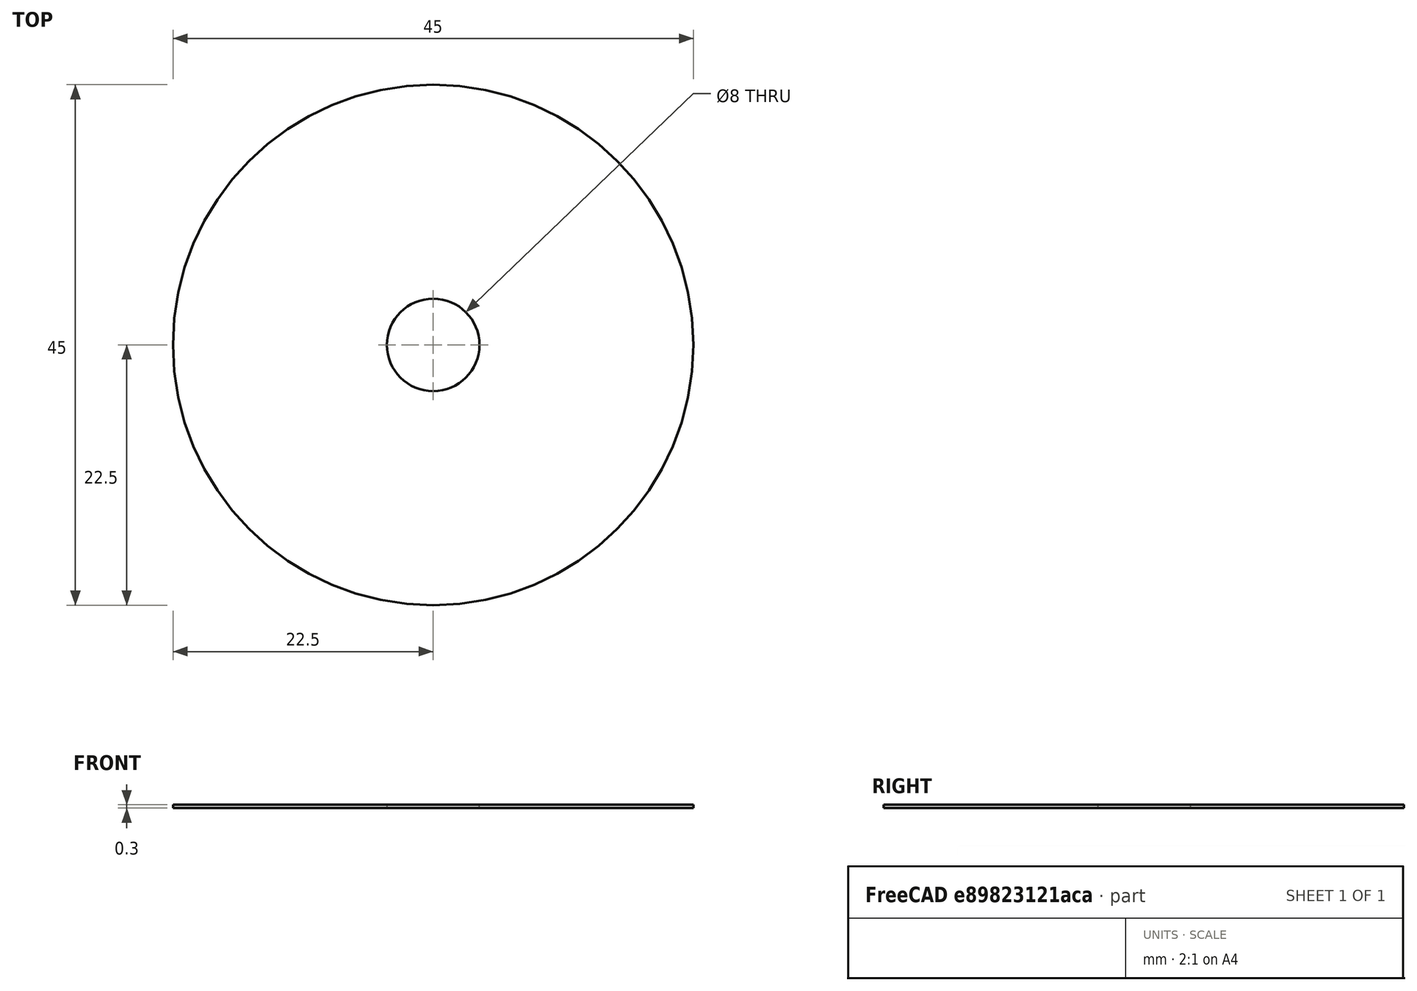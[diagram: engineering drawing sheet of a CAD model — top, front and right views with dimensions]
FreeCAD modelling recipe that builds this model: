
FCSTD DOCUMENT  (FreeCAD 1.0R39109 (Git))
Label: Лезвие
License: All rights reserved
LicenseURL: https://en.wikipedia.org/wiki/All_rights_reserved
objects: Sketcher::SketchObject×1, PartDesign::Pad×1, PartDesign::Body×1
note: 6 computed .brp shape members not serialized (recipe doc carries the construction recipe); baked Part::Feature solids carry a one-line shape summary decoded from their .brp

FEATURE [Sketcher::SketchObject] Sketch
  ArcFitTolerance = 1e-06
  AttachmentSupport = -> [XY_Plane]
  FullyConstrained = true
  MakeInternals = false
  MapMode = 5
  sketch-geometry (2):
    g0: Circle CenterX=0 CenterY=0 CenterZ=0 NormalX=0 NormalY=0 NormalZ=1 AngleXU=0 Radius=22.5
    g1: Circle CenterX=0 CenterY=0 CenterZ=0 NormalX=0 NormalY=0 NormalZ=1 AngleXU=0 Radius=4
  constraints (4):
    c: Diameter(g0) = 45
    c: Coincident(g0,g-1)
    c: Diameter(g1) = 8
    c: Coincident(g1,g0)
FEATURE [PartDesign::Pad] Pad
  Direction = (0,0,1)
  Length = 0.3
  Length2 = 10
  Profile = -> Sketch
  ReferenceAxis = -> Sketch [N_Axis]
  Refine = true
  Suppressed = false
  Type = 0
FEATURE [PartDesign::Body] Body
  AllowCompound = false
  Group = -> [Sketch,Pad]
  Origin = -> Origin
  Tip = -> Pad
